# Revit family: RSV_8-11mm_150_10Ø_12Ø_test
name_source: partatom
category: Generic Models
units: mm (PartAtom-declared; Revit-internal decimal feet)

## family parameters
Always vertical = No
Can host rebar = Yes
Cut with Voids When Loaded = No
Part Type = Normal
Room Calculation Point = No
Round Connector Dimension = Use Diameter
Shared = No
Work Plane-Based = Yes

## types (5) — shared parameters
CenterToCenter = 150 mm
Default Elevation = 1219 mm
Manufacturer = Recostal
Model = RSV
Rot own axis = 0.00°
Rot_XY_shared = 0.00°
Rot_XZ_shared = 90.00°
Total Length = 1250 mm  [stored 4.10105 ft]
URL = https://www.haucon.fi
Width Box 2 = 49 mm
Width Box 3 = 68 mm
Width Box 4 = 68 mm

## per-type parameters (varying)
| type | Diameter Rebar | Length rebar | Width Box | Width rebar |
| RSV 8 10Ø | 10 mm  [stored 0.0328084 ft] | 540 mm | 29 mm  [stored 0.0951444 ft] | 25 mm  [stored 0.082021 ft] |
| RSV 11 10Ø 150 | 10 mm  [stored 0.0328084 ft] | 540 mm | 59 mm | 55 mm |
| RSV 8 8Ø | 8 mm  [stored 0.0262467 ft] | 470 mm  [stored 1.54199 ft] | 29 mm  [stored 0.0951444 ft] | 25 mm  [stored 0.082021 ft] |
| RSV 11 8Ø 150 | 8 mm  [stored 0.0262467 ft] | 470 mm  [stored 1.54199 ft] | 59 mm | 55 mm |
| RSV 11 12Ø 150 | 12 mm  [stored 0.0393701 ft] | 610 mm | 59 mm | 55 mm |

note: [stored X ft] marks values corroborated as IEEE doubles in the binary element streams (Revit-internal decimal feet)

## geometry (parser evidence)
native form markers: Sweep x17
no freeform markers — native parametric forms only
